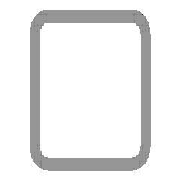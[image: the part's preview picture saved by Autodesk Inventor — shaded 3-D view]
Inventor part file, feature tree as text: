
AUTODESK INVENTOR PART (.ipt)
format: ipt  version: 2025.1 (Build 291241020, 241B)  size: 134,144 bytes
history: native  units: mm (DEFAULTED — no unit token found)
features: other x4, sketch x1, plane x1
ambient origin geometry x8: Origin, YZ Plane, XZ Plane, XY Plane, X Axis, Y Axis, Z Axis, Center Point
bodies: Solid1 (feature_tree), Body (feature_tree)
feature tree (6):
  parser-record x1  (decoder bookkeeping rows leaked as tree rows — omitted from the tree; the rows remain in map.json)
  other  "Driven Length"
  other  "Start Plane"
  other  "End Plane"
  sketch  "Sketch3"  dims[d3=950.0mm d4=0.0mm d7=8.0mm d9=100.0mm d11=100.0mm d12=4.0mm d13=50.0mm d14=1000.0mm d15=50.0mm d16=50.0mm d17=90.0deg d18=950.0mm]
  plane  "Work Plane3"
